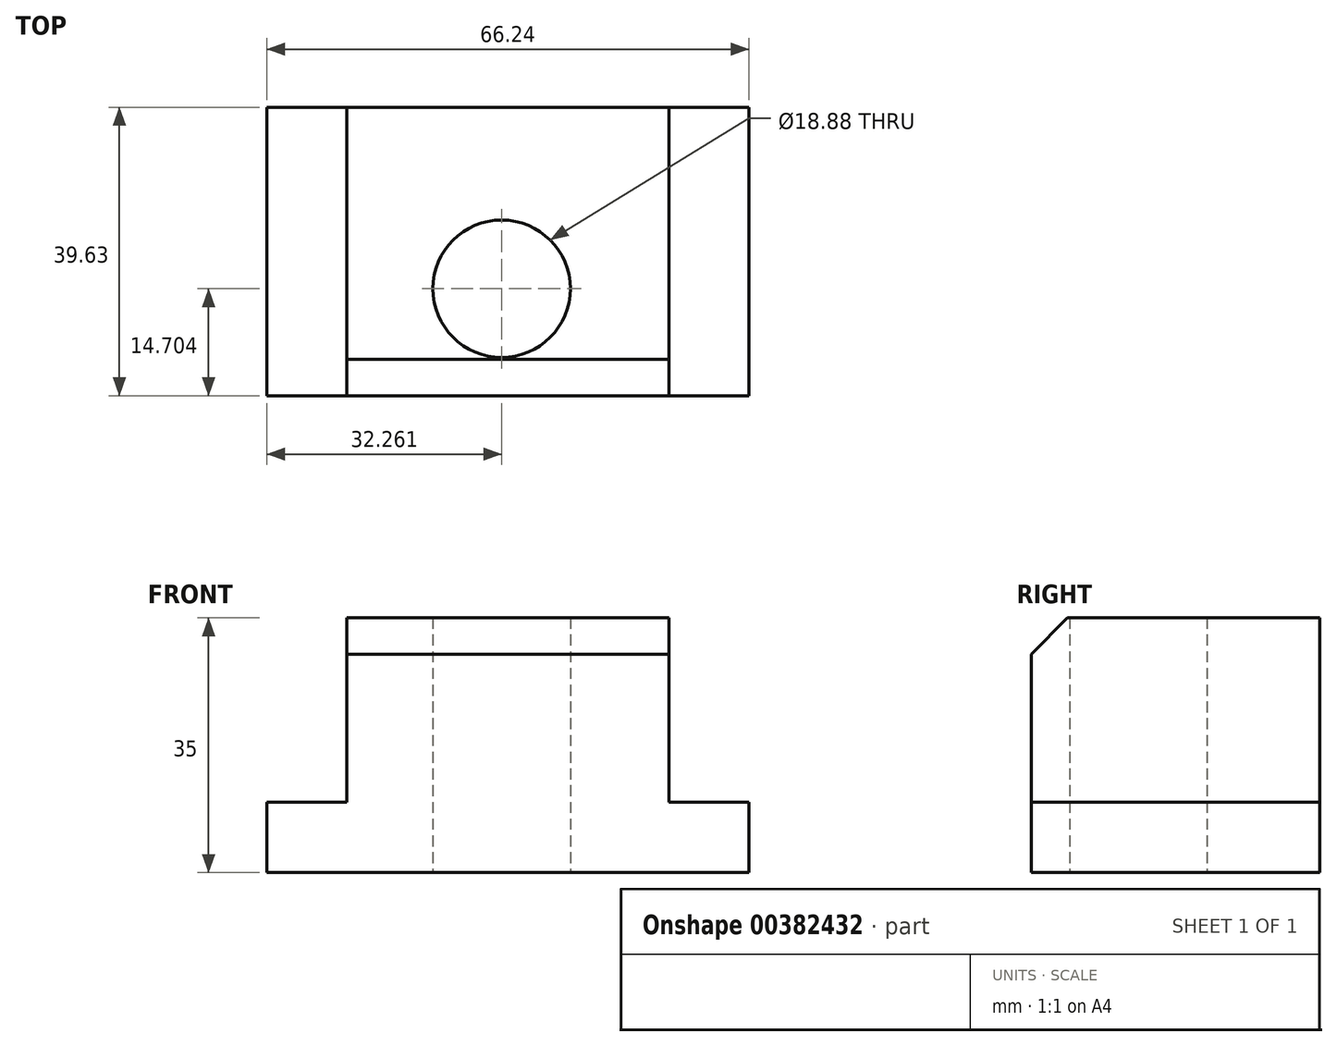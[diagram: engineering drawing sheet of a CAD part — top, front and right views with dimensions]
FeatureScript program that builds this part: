
annotation { "Feature Type Name" : "Feature", "Feature Type Description" : "" }
export const myFeature = defineFeature(function(context is Context, id is Id, definition is map)
    precondition{}
    {
        {
            var Q0;
            Q0=qCreatedBy(makeId("Top.planeOp"),FACE);
            var sketch = newSketch(context, id + "F0", { "sketchPlane" : qUnion([Q0])});
            skLineSegment(sketch, "E0", {"start": v(26.99, 52.57) * mm, "end": v(26.99, 12.94) * mm});
            skLineSegment(sketch, "E1", {"start": v(26.99, 12.94) * mm, "end": v(-39.25, 12.94) * mm});
            skLineSegment(sketch, "E2", {"start": v(-39.25, 12.94) * mm, "end": v(-39.25, 52.57) * mm});
            skLineSegment(sketch, "E3", {"start": v(-39.25, 52.57) * mm, "end": v(26.99, 52.57) * mm});
            skLineSegment(sketch, "E4", {"start": v(-28.25, 52.57) * mm, "end": v(-28.25, 12.94) * mm});
            skLineSegment(sketch, "E5", {"start": v(15.99, 52.57) * mm, "end": v(15.99, 12.94) * mm});
            skSolve(sketch);
        }
        {
            var Q0;
            {var subQ0=sQuery(id+"F0.wireOp",EDGE,"E4");Q0=makeQuery(id+"F0.imprint","IMPRINT",FACE,{"disambiguationData":[TD([[makeQuery(id+"F0.imprint","IMPRINT",EDGE,{"derivedFrom":subQ0}),1.0]])]});}
            extrude(context, id + "F1", {"entities" : qUnion([Q0]), "depth" : 35 * mm});
        }
        {
            var Q0;
            {var subQ0=sQuery(id+"F0.wireOp",EDGE,"E0");Q0=makeQuery(id+"F0.imprint","IMPRINT",FACE,{"disambiguationData":[TD([[makeQuery(id+"F0.imprint","IMPRINT",EDGE,{"derivedFrom":subQ0}),-1.0]])]});}
            var Q1;
            {var subQ0=sQuery(id+"F0.wireOp",EDGE,"E2");Q1=makeQuery(id+"F0.imprint","IMPRINT",FACE,{"disambiguationData":[TD([[makeQuery(id+"F0.imprint","IMPRINT",EDGE,{"derivedFrom":subQ0}),-1.0]])]});}
            extrude(context, id + "F2", {"entities" : qUnion([Q0, Q1]), "operationType" : NewBodyOperationType.ADD, "depth" : 9.65 * mm});
        }
        {
            var Q0;
            Q0=makeQuery(id+"F1.opExtrude","CAP_EDGE",EDGE,{"disambiguationData":[OSD([sQuery(id+"F0.wireOp",EDGE,"E1")])],"isStart":false});
            chamfer(context, id + "F3", {"entities" : qUnion([Q0]), "width" : 5 * mm, "tangentPropagation" : true});
        }
        {
            var Q0;
            Q0=qCreatedBy(makeId("Right.planeOp"),FACE);
            var sketch = newSketch(context, id + "F4", { "sketchPlane" : qUnion([Q0])});
            skCircle(sketch, "E6", {"center": v(21.8, 29.3) * mm, "radius": 2.37 * mm});
            skSolve(sketch);
        }
        {
            var Q0;
            Q0 = qSketchRegion(id + "F4", true);
            extrude(context, id + "F5", {"entities" : qUnion([Q0]), "operationType" : NewBodyOperationType.ADD, "endBound" : BoundingType.SYMMETRIC, "depth" : 25.4 * mm});
        }
        {
            var Q0;
            Q0=qCreatedBy(makeId("Top.planeOp"),FACE);
            var sketch = newSketch(context, id + "F6", { "sketchPlane" : qUnion([Q0])});
            skCircle(sketch, "E7", {"center": v(-6.99, 27.64) * mm, "radius": 9.44 * mm});
            skSolve(sketch);
        }
        {
            var Q0;
            Q0 = qSketchRegion(id + "F6", true);
            extrude(context, id + "F7", {"entities" : qUnion([Q0]), "operationType" : NewBodyOperationType.REMOVE, "endBound" : BoundingType.SYMMETRIC, "depth" : 83.82 * mm});
        }
    });
